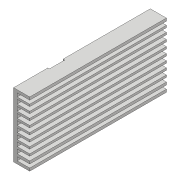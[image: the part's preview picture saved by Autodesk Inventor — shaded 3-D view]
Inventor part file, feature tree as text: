
AUTODESK INVENTOR PART (.ipt)
format: ipt  version: 2018 (Build 220112000, 112)  size: 178,688 bytes
history: native  units: mm
features: extrude x6, sketch x6, projected_geometry x3, mirror x1, pattern_linear x1
ambient origin geometry x8: Origin, YZ Plane, XZ Plane, XY Plane, X Axis, Y Axis, Z Axis, Center Point
bodies: Solid1 (feature_tree)
feature tree (17):
  extrude  "Extrusion1"  Depth=40.0mm
  extrude  "Extrusion2"  Depth=1.7mm
  mirror  "Mirror1"
  extrude  "Extrusion3"  Depth=2.2mm
  pattern_linear  "Rectangular Pattern1"  Spacing1=85.0mm  [1 undecoded]
  extrude  "Extrusion4"  Depth=3.82mm
  extrude  "Extrusion5"  Depth=1.0mm TaperAngle=0.0deg
  extrude  "Extrusion7"  Depth=1.0mm TaperAngle=0.0deg
  sketch  "Sketch1"  dims[d0=20.0mm d1=40.0mm]
  sketch  "Sketch2"  dims[d2=85.0mm d3=0.0mm d4=1.7mm]
  projected_geometry  "Projected Loop1"
  sketch  "Sketch3"  dims[d5=4.2mm d6=2.2mm]
  projected_geometry  "Projected Loop2"
  sketch  "Sketch4"  dims[d7=85.0mm d8=0.0mm]
  projected_geometry  "Projected Loop3"
  sketch  "Sketch5"  dims[d9=1.3mm]
  sketch  "Sketch7"  dims[d10=2.52mm d11=85.0mm d12=0.0mm d13=80.0mm d15=3.82mm d16=2.0mm d17=0.0mm d18=8.0mm d19=0.0mm d24=9.525mm d25=3.0mm d26=26.0mm d29=10.0mm d30=1.0mm d31=0.0mm]
note: 1 required parameter value undecoded (feature->parameter linkage not recoverable at this tier; creation-order binding heuristic only, values carry confidence <= 0.55)
